# Revit family: ASL_Designline_Skirting_Wall_Starter_64mm Stud_18mm Gib_BS
name_source: partatom
category: Detail Items
revit_build: Autodesk Revit 2018 (Build: 20170223_1515(x64)
units: mm (PartAtom-declared; Revit-internal decimal feet)

## family parameters
Rotate with component = No
Section Shape = Not Defined
Shared = Yes

## types (3) — shared parameters
Manufacturer = Aluminate Solutions Limited
Technical Info = www.aluminate.nz

## per-type parameters (varying)
| type | Skirting_100 | Skirting_120 | Skirting_150 | Type Comments |
| Skirting 100mm | Yes | No | No | ASL Designline Wall Starter With 100mm Skirting for ASL 410 Headsection 64mm Stud 18mm Gib Bothside Wall |
| Skirting 120mm | No | Yes | No | ASL Designline Wall Starter With 120mm Skirting for ASL 410 Headsection 64mm Stud 18mm Gib Bothside Wall |
| Skirting 150mm | No | No | Yes | ASL Designline Wall Starter With 150mm Skirting for ASL 410 Headsection 64mm Stud 18mm Gib Bothside Wall |

## geometry (parser evidence)
native form markers: Sweep x5
no freeform markers — native parametric forms only
